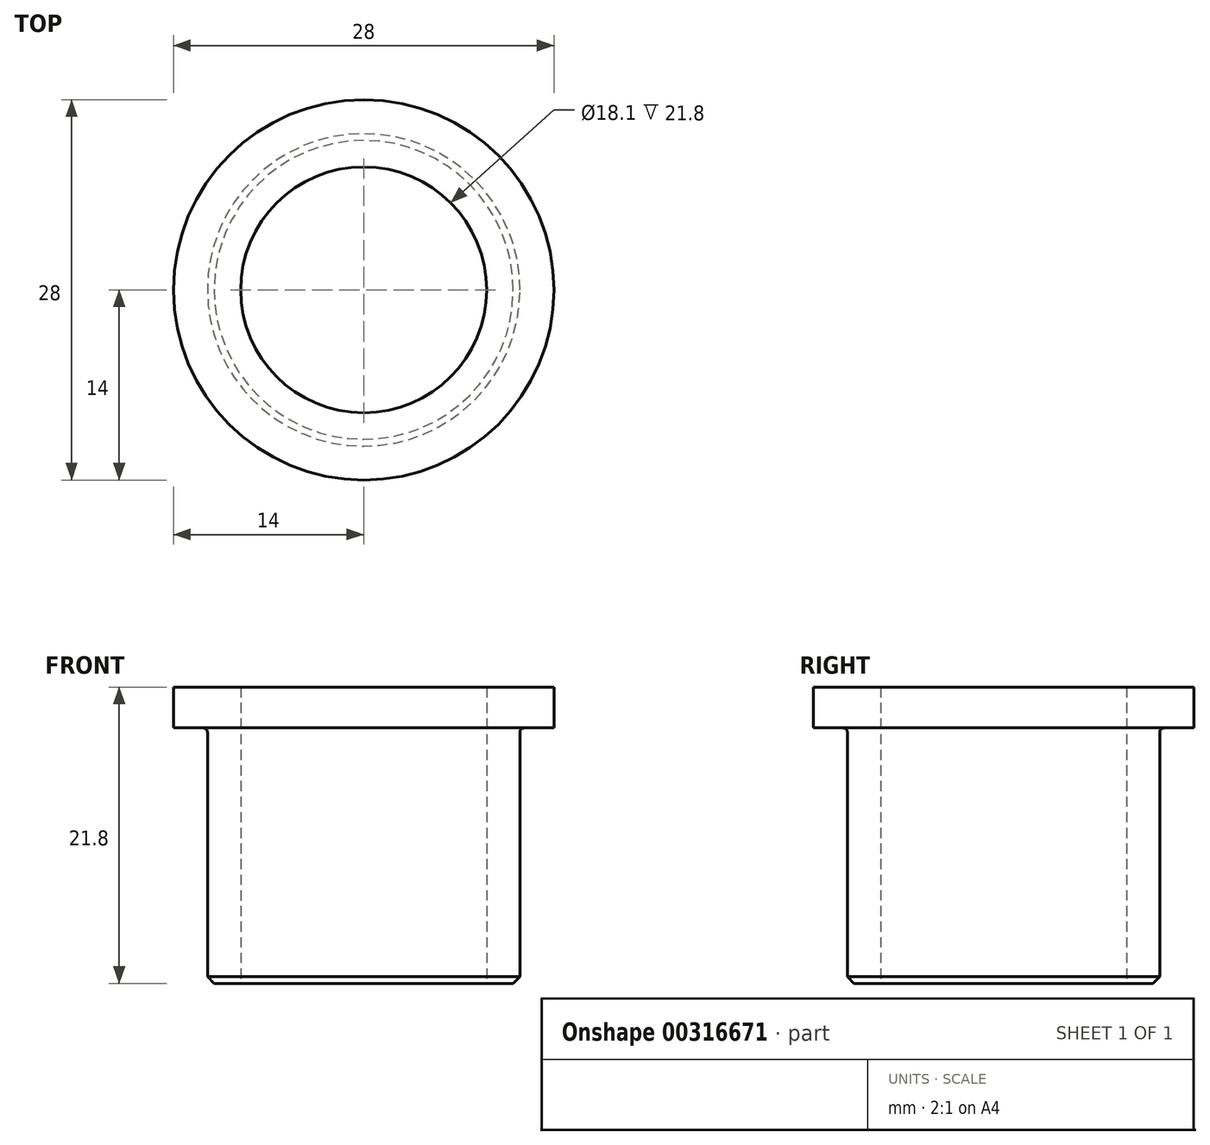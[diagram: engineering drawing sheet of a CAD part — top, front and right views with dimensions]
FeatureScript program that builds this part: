
annotation { "Feature Type Name" : "Feature", "Feature Type Description" : "" }
export const myFeature = defineFeature(function(context is Context, id is Id, definition is map)
    precondition{}
    {
        {
            assignVariable(context, id + "F0", {"name" : "Fillet", "anyValue" : 0.3});
        }
        {
            assignVariable(context, id + "F1", {"name" : "Chamfer", "anyValue" : 0.5});
        }
        {
            var Q0;
            Q0=qCreatedBy(makeId("Front.planeOp"),FACE);
            var sketch = newSketch(context, id + "F2", { "sketchPlane" : qUnion([Q0])});
            skLineSegment(sketch, "E0", {"start": v(0, 0) * mm, "end": v(0, 21.8) * mm, "construction": true});
            skLineSegment(sketch, "E1", {"start": v(-14, 21.8) * mm, "end": v(-14, 18.8) * mm});
            skLineSegment(sketch, "E2", {"start": v(-14, 18.8) * mm, "end": v(-11.5, 18.8) * mm});
            skLineSegment(sketch, "E3", {"start": v(-11.5, 18.8) * mm, "end": v(-11.5, 0) * mm});
            skLineSegment(sketch, "E4", {"start": v(-11.5, 0) * mm, "end": v(-9.05, 0) * mm});
            skLineSegment(sketch, "E5", {"start": v(-9.05, 0) * mm, "end": v(-9.05, 21.8) * mm});
            skLineSegment(sketch, "E6", {"start": v(-14, 21.8) * mm, "end": v(-9.05, 21.8) * mm});
            skSolve(sketch);
        }
        {
            var Q0;
            Q0=makeQuery(id+"F2.imprint","IMPRINT",FACE,{"disambiguationData":[TD([[makeQuery(id+"F2.imprint","IMPRINT",EDGE,{"derivedFrom":sQuery(id+"F2.wireOp",EDGE,"E1")}),1.0]])]});
            var Q1;
            Q1=sQuery(id+"F2.wireOp",EDGE,"E0");
            revolve(context, id + "F3", {"entities" : qUnion([Q0]), "axis" : qUnion([Q1]), "revolveType" : RevolveType.FULL});
        }
        {
            var Q0;
            Q0=makeQuery(id+"F3.opRevolve","SWEPT_EDGE",EDGE,{"disambiguationData":[OSD([sQuery(id+"F2.wireOp",EDGE,"E2"),sQuery(id+"F2.wireOp",EDGE,"E3")])]});
            fillet(context, id + "F4", {"entities" : qUnion([Q0]), "radius" : (getVariable(context, 'Fillet')) * mm, "tangentPropagation" : true, "allowEdgeOverflow" : false});
        }
        {
            var Q0;
            Q0=makeQuery(id+"F3.opRevolve","SWEPT_EDGE",EDGE,{"disambiguationData":[OSD([sQuery(id+"F2.wireOp",EDGE,"E3"),sQuery(id+"F2.wireOp",EDGE,"E4")])]});
            chamfer(context, id + "F5", {"entities" : qUnion([Q0]), "width" : (getVariable(context, 'Chamfer')) * mm, "tangentPropagation" : true});
        }
    });
